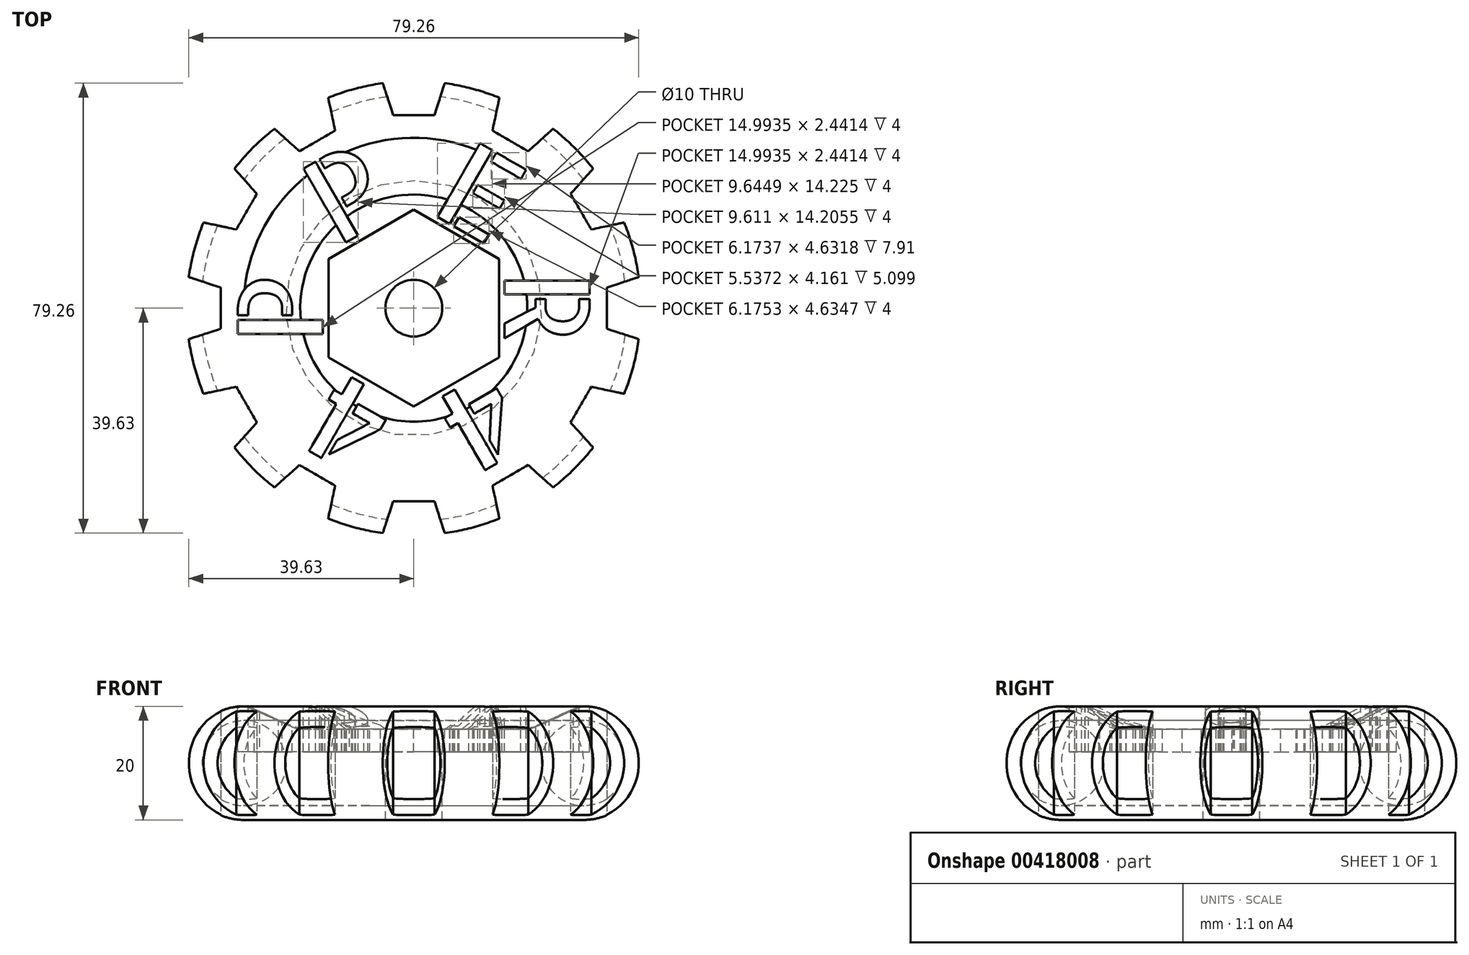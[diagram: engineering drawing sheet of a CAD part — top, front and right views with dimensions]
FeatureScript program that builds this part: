
annotation { "Feature Type Name" : "Feature", "Feature Type Description" : "" }
export const myFeature = defineFeature(function(context is Context, id is Id, definition is map)
    precondition{}
    {
        {
            var Q0;
            Q0=qCreatedBy(makeId("Front.planeOp"),FACE);
            var sketch = newSketch(context, id + "F0", { "sketchPlane" : qUnion([Q0])});
            skLineSegment(sketch, "E0.bottom", {"start": v(0, 0) * mm, "end": v(-30, 0) * mm});
            skLineSegment(sketch, "E0.left", {"start": v(0, 0) * mm, "end": v(0, 16) * mm});
            skArc(sketch, "E1", {"start": v(-30, 20) * mm, "mid": v(-40, 10) * mm, "end": v(-30, 0) * mm});
            skPoint(sketch, "E2", {"position": v(0, 16) * mm});
            skPoint(sketch, "E3", {"position": v(-20, 16) * mm});
            skLineSegment(sketch, "E4", {"start": v(0, 16) * mm, "end": v(-20, 16) * mm});
            skFitSpline(sketch, "E5", {"points": [v(-30, 20) * mm, v(-20, 16) * mm], "startDerivative": vector(3.41, -0.02) * mm, "endDerivative": vector(4.32, 0.11) * mm});
            skSolve(sketch);
        }
        {
            var Q0;
            Q0=makeQuery(id+"F0.imprint","IMPRINT",FACE,{"disambiguationData":[TD([[makeQuery(id+"F0.imprint","IMPRINT",EDGE,{"derivedFrom":sQuery(id+"F0.wireOp",EDGE,"E0.bottom")}),-1.0]])]});
            var Q1;
            Q1=sQuery(id+"F0.wireOp",EDGE,"E0.left");
            revolve(context, id + "F1", {"entities" : qUnion([Q0]), "axis" : qUnion([Q1]), "revolveType" : RevolveType.FULL});
        }
        {
            var Q0;
            Q0=qCreatedBy(makeId("Front.planeOp"),FACE);
            var sketch = newSketch(context, id + "F2", { "sketchPlane" : qUnion([Q0])});
            skCircle(sketch, "E6", {"center": v(-30, 10) * mm, "radius": 7.5 * mm});
            skSolve(sketch);
        }
        {
            var Q0;
            Q0=qCreatedBy(makeId("Top.planeOp"),FACE);
            var Q1;
            Q1=sQuery(id+"F0.wireOp",VERTEX,"E5.start");
            cPlane(context, id + "F3", {"entities" : qUnion([Q0, Q1]), "cplaneType" : CPlaneType.PLANE_POINT, "offset" : 10.8 * mm, "width" : 150 * mm, "height" : 150 * mm});
        }
        {
            var Q0;
            Q0=qCreatedBy(id+"F3.planeOp",FACE);
            var sketch = newSketch(context, id + "F4", { "sketchPlane" : qUnion([Q0])});
            skCircle(sketch, "E7.cCircle", {"center": v(0, 0) * mm, "radius": 15 * mm, "construction": true});
            skLineSegment(sketch, "E7.0", {"start": v(-15, 8.66) * mm, "end": v(0, 17.32) * mm});
            skLineSegment(sketch, "E7.1", {"start": v(0, 17.32) * mm, "end": v(15, 8.66) * mm});
            skLineSegment(sketch, "E7.2", {"start": v(15, 8.66) * mm, "end": v(15, -8.66) * mm});
            skLineSegment(sketch, "E7.3", {"start": v(15, -8.66) * mm, "end": v(0, -17.32) * mm});
            skLineSegment(sketch, "E7.4", {"start": v(0, -17.32) * mm, "end": v(-15, -8.66) * mm});
            skLineSegment(sketch, "E7.5", {"start": v(-15, -8.66) * mm, "end": v(-15, 8.66) * mm});
            skPoint(sketch, "E7.0.midPoint", {"position": v(-7.5, 13) * mm});
            skText(sketch, "E8", { "text": "P", "fontName": "AllertaStencil-Regular.ttf"});
            skText(sketch, "E9", { "text": "P", "fontName": "AllertaStencil-Regular.ttf"});
            skText(sketch, "E10", { "text": "E", "fontName": "AllertaStencil-Regular.ttf"});
            skText(sketch, "E11", { "text": "4", "fontName": "AllertaStencil-Regular.ttf"});
            skText(sketch, "E12", { "text": "R", "fontName": "AllertaStencil-Regular.ttf"});
            skText(sketch, "E13", { "text": "4", "fontName": "AllertaStencil-Regular.ttf"});
            skLineSegment(sketch, "E14", {"start": v(0, 0) * mm, "end": v(7.5, -13) * mm, "construction": true});
            skLineSegment(sketch, "E15", {"start": v(0, 0) * mm, "end": v(15, 0) * mm, "construction": true});
            skLineSegment(sketch, "E16", {"start": v(0, 0) * mm, "end": v(-7.5, 13) * mm, "construction": true});
            skLineSegment(sketch, "E17", {"start": v(0, 0) * mm, "end": v(-15, 0) * mm, "construction": true});
            skLineSegment(sketch, "E18", {"start": v(0, 0) * mm, "end": v(-7.5, -13) * mm, "construction": true});
            skLineSegment(sketch, "E19", {"start": v(0, 0) * mm, "end": v(7.5, 13) * mm, "construction": true});
            skCircle(sketch, "E20", {"center": v(0, 0) * mm, "radius": 5 * mm});
            const initialGuessF4  = {"E8": [-0.016, -0.0064, 0, 1, 0.015], "E9": [-0.01354, 0.01066, 0.86603, 0.5, 0.015], "E10": [0.0025, 0.01703, 0.86603, -0.5, 0.015], "E11": [-0.0025, -0.01703, -0.86603, 0.5, 0.015], "E12": [0.016, 0.0067, 0, -1, 0.015], "E13": [0.0135, -0.01068, -0.86603, -0.5, 0.015]};
            skSetInitialGuess(sketch, initialGuessF4);
            skSolve(sketch);
        }
        {
            var Q0;
            Q0=qSketchRegion(id+"F4",true);
            extrude(context, id + "F5", {"entities" : qUnion([Q0]), "operationType" : NewBodyOperationType.REMOVE, "oppositeDirection" : true, "depth" : 8 * mm});
        }
        {
            var Q0;
            Q0=qSketchRegion(id+"F2",true);
            var Q1;
            Q1=sQuery(id+"F0.wireOp",EDGE,"E0.left");
            revolve(context, id + "F6", {"entities" : qUnion([Q0]), "axis" : qUnion([Q1]), "revolveType" : RevolveType.FULL});
        }
        {
            var Q0;
            Q0=qCreatedBy(makeId("Top.planeOp"),FACE);
            var sketch = newSketch(context, id + "F7", { "sketchPlane" : qUnion([Q0])});
            skCircle(sketch, "E21.cCircle", {"center": v(0, 39) * mm, "radius": 5 * mm, "construction": true});
            skLineSegment(sketch, "E21.0", {"start": v(3.63, 34) * mm, "end": v(-3.63, 34) * mm});
            skLineSegment(sketch, "E21.1", {"start": v(-3.63, 34) * mm, "end": v(-5.88, 40.9) * mm});
            skLineSegment(sketch, "E21.2", {"start": v(-5.88, 40.9) * mm, "end": v(0, 45.18) * mm});
            skLineSegment(sketch, "E21.3", {"start": v(0, 45.18) * mm, "end": v(5.88, 40.9) * mm});
            skLineSegment(sketch, "E21.4", {"start": v(5.88, 40.9) * mm, "end": v(3.63, 34) * mm});
            skPoint(sketch, "E21.0.midPoint", {"position": v(0, 34) * mm});
            skSolve(sketch);
        }
        {
            var Q0;
            Q0=makeQuery(id+"F7.imprint","IMPRINT",FACE,{"disambiguationData":[TD([[makeQuery(id+"F7.imprint","IMPRINT",EDGE,{"derivedFrom":sQuery(id+"F7.wireOp",EDGE,"E21.0")}),-1.0]])]});
            extrude(context, id + "F8", {"entities" : qUnion([Q0]), "endBound" : BoundingType.SYMMETRIC, "depth" : 100 * mm});
        }
        {
            var Q0;
            Q0=makeQuery(id+"F8.opExtrude","SWEPT_BODY",BODY,{"disambiguationData":[OSD([sQuery(id+"F7.wireOp",EDGE,"E21.0"),sQuery(id+"F7.wireOp",EDGE,"E21.1"),sQuery(id+"F7.wireOp",EDGE,"E21.2"),sQuery(id+"F7.wireOp",EDGE,"E21.3"),sQuery(id+"F7.wireOp",EDGE,"E21.4")])]});
            var Q1;
            Q1=sQuery(id+"F0.wireOp",EDGE,"E0.left");
            circularPattern(context, id + "F9", {"operationType" : NewBodyOperationType.REMOVE, "entities" : qUnion([Q0]), "axis" : qUnion([Q1]), "angle" : 360 * degree, "instanceCount" : 12, "equalSpace" : true, "isCentered" : true});
        }
        {
            var Q0;
            Q0=makeQuery(id+"F5.boolean.opBoolean","SPLIT",FACE,{"disambiguationData":[TD([makeQuery(id+"F5.opExtrude","SWEPT_FACE",FACE,{"disambiguationData":[OSD([sQuery(id+"F4.wireOp",EDGE,"E20")])]})])],"derivedFrom":makeQuery(id+"F1.opRevolve","SWEPT_FACE",FACE,{"disambiguationData":[OSD([sQuery(id+"F0.wireOp",EDGE,"E4")])]})});
            extrude(context, id + "F10", {"entities" : qUnion([Q0]), "operationType" : NewBodyOperationType.REMOVE, "oppositeDirection" : true, "depth" : 25 * mm});
        }
    });
